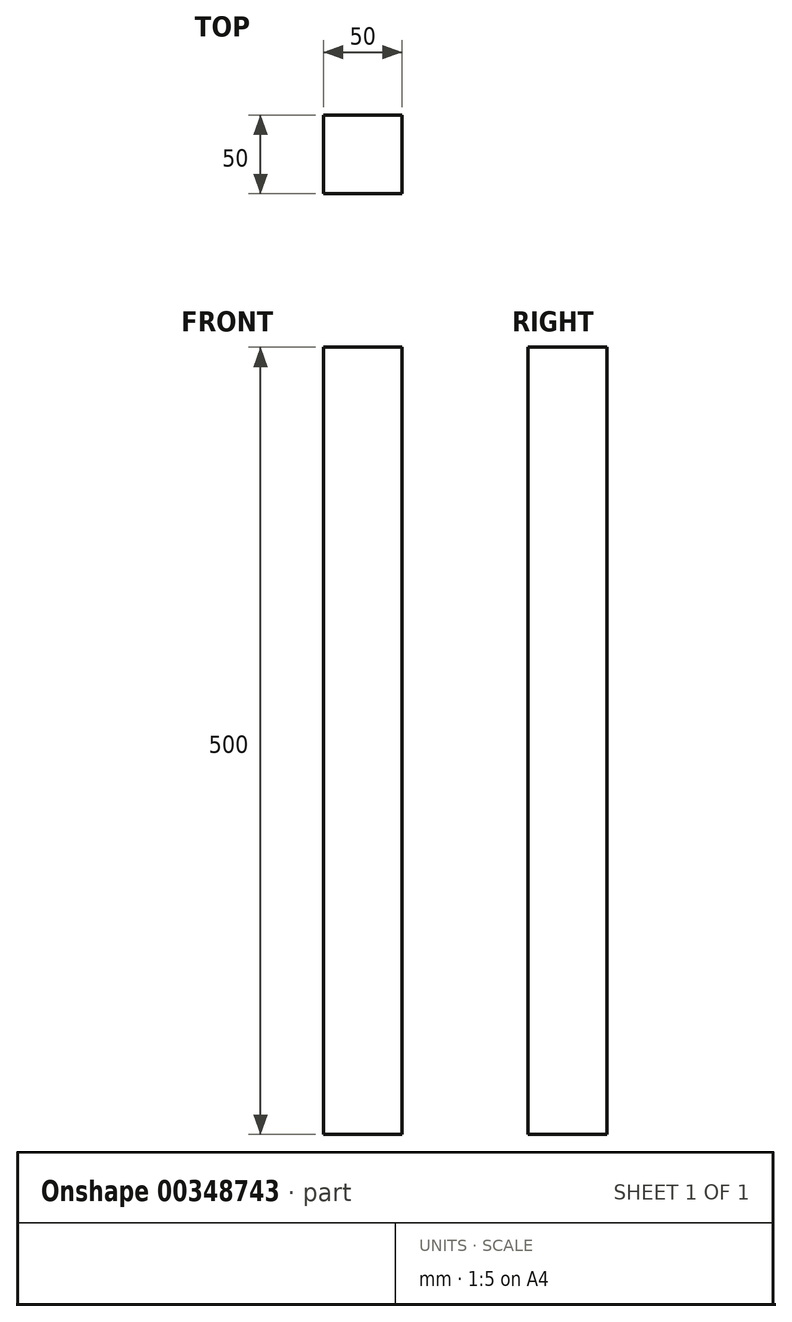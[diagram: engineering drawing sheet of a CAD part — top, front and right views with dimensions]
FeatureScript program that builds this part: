
annotation { "Feature Type Name" : "Feature", "Feature Type Description" : "" }
export const myFeature = defineFeature(function(context is Context, id is Id, definition is map)
    precondition{}
    {
        {
            var Q0;
            Q0=qCreatedBy(makeId("Top.planeOp"),FACE);
            var sketch = newSketch(context, id + "F0", { "sketchPlane" : qUnion([Q0])});
            skLineSegment(sketch, "E0.bottom", {"start": v(0, 0) * mm, "end": v(-50, 0) * mm});
            skLineSegment(sketch, "E0.top", {"start": v(0, 50) * mm, "end": v(-50, 50) * mm});
            skLineSegment(sketch, "E0.left", {"start": v(0, 0) * mm, "end": v(0, 50) * mm});
            skLineSegment(sketch, "E0.right", {"start": v(-50, 0) * mm, "end": v(-50, 50) * mm});
            skSolve(sketch);
        }
        {
            var Q0;
            Q0 = qSketchRegion(id + "F0", true);
            extrude(context, id + "F1", {"entities" : qUnion([Q0]), "depth" : 500 * mm});
        }
    });
